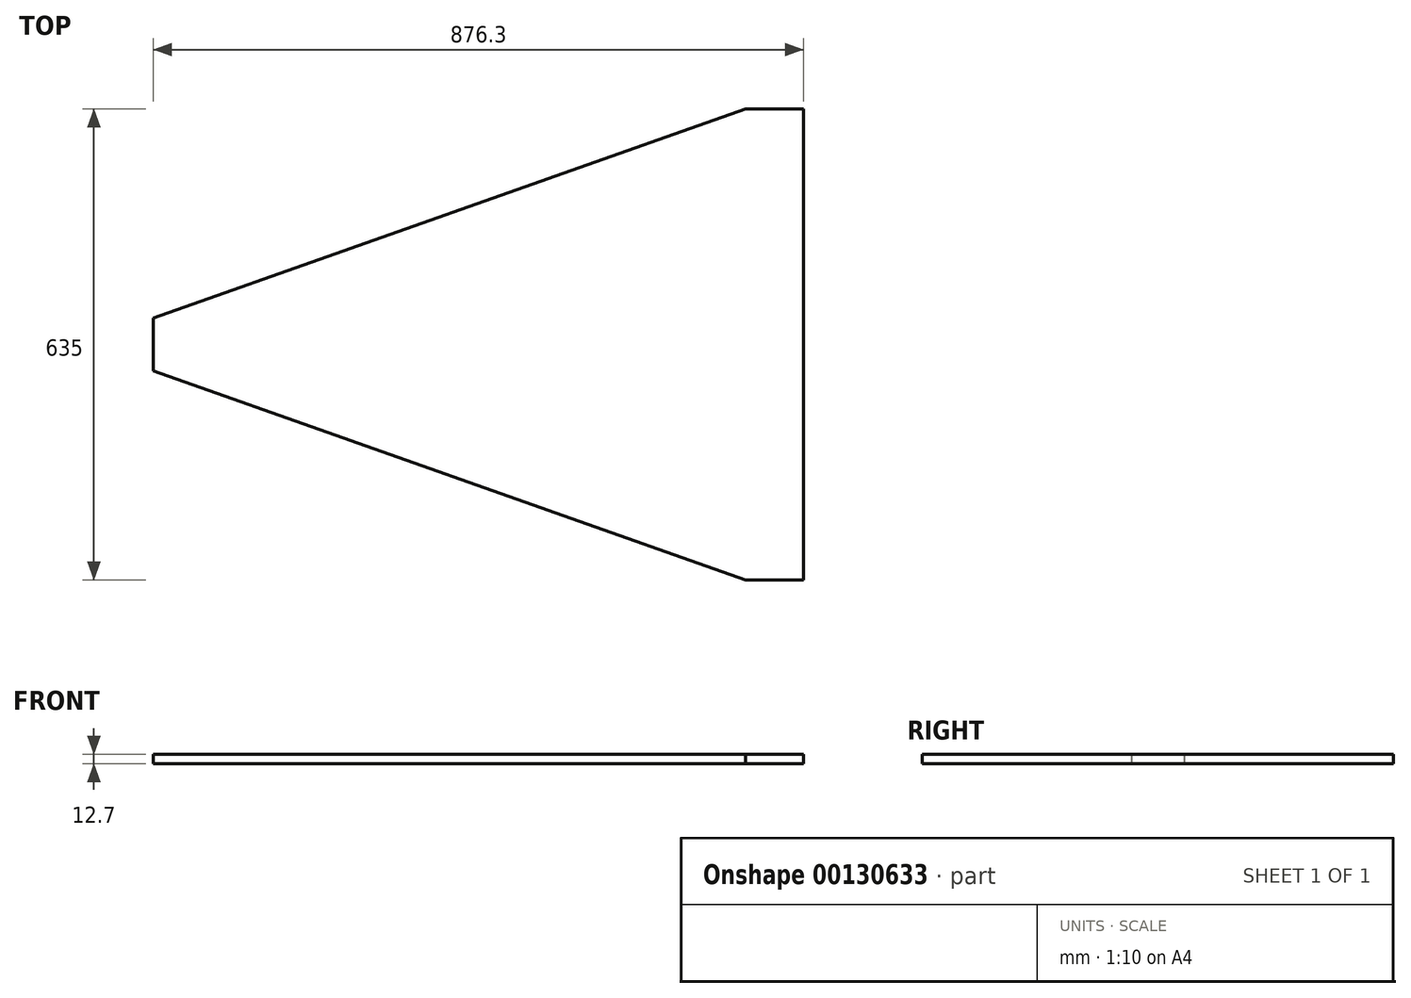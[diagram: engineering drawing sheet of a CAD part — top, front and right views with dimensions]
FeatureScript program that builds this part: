
annotation { "Feature Type Name" : "Feature", "Feature Type Description" : "" }
export const myFeature = defineFeature(function(context is Context, id is Id, definition is map)
    precondition{}
    {
        {
            var Q0;
            Q0=qCreatedBy(makeId("Top.planeOp"),FACE);
            var sketch = newSketch(context, id + "F0", { "sketchPlane" : qUnion([Q0])});
            skLineSegment(sketch, "E0.bottom", {"start": v(0, 0) * mm, "end": v(-78.38, 0) * mm});
            skLineSegment(sketch, "E0.top", {"start": v(0, 635) * mm, "end": v(-78.38, 635) * mm});
            skLineSegment(sketch, "E0.left", {"start": v(0, 0) * mm, "end": v(0, 635) * mm});
            skLineSegment(sketch, "E0.right", {"start": v(-114.3, 12.7) * mm, "end": v(-114.3, 622.3) * mm});
            skLineSegment(sketch, "E1", {"start": v(-114.3, 317.5) * mm, "end": v(-876.3, 317.5) * mm});
            skLineSegment(sketch, "E2", {"start": v(-78.38, 635) * mm, "end": v(-876.3, 352.9) * mm});
            skLineSegment(sketch, "E3", {"start": v(-78.38, 0) * mm, "end": v(-876.3, 282.1) * mm});
            skLineSegment(sketch, "E4", {"start": v(-876.3, 317.5) * mm, "end": v(-876.3, 352.9) * mm});
            skLineSegment(sketch, "E5", {"start": v(-876.3, 317.5) * mm, "end": v(-876.3, 282.1) * mm});
            skLineSegment(sketch, "E6", {"start": v(-876.3, 282.1) * mm, "end": v(-976.4, 317.5) * mm});
            skPoint(sketch, "E7.orphan", {"position": v(-114.3, 635) * mm});
            skPoint(sketch, "E8.end.orphan", {"position": v(-114.3, 12.7) * mm});
            skPoint(sketch, "E9.orphan", {"position": v(-114.3, 0) * mm});
            skSolve(sketch);
        }
        {
            var Q0;
            {var subQ0=sQuery(id+"F0.wireOp",EDGE,"E2");Q0=makeQuery(id+"F0.imprint","IMPRINT",FACE,{"disambiguationData":[TD([[makeQuery(id+"F0.imprint","IMPRINT",EDGE,{"derivedFrom":subQ0}),1.0]])]});}
            var Q1;
            {var subQ0=sQuery(id+"F0.wireOp",EDGE,"E3");Q1=makeQuery(id+"F0.imprint","IMPRINT",FACE,{"disambiguationData":[TD([[makeQuery(id+"F0.imprint","IMPRINT",EDGE,{"derivedFrom":subQ0}),-1.0]])]});}
            var Q2;
            Q2=makeQuery(id+"F0.imprint","IMPRINT",FACE,{"disambiguationData":[TD([[makeQuery(id+"F0.imprint","IMPRINT",EDGE,{"derivedFrom":sQuery(id+"F0.wireOp",EDGE,"E0.bottom")}),-1.0]])]});
            extrude(context, id + "F1", {"entities" : qUnion([Q0, Q1, Q2]), "depth" : 12.7 * mm});
        }
    });
